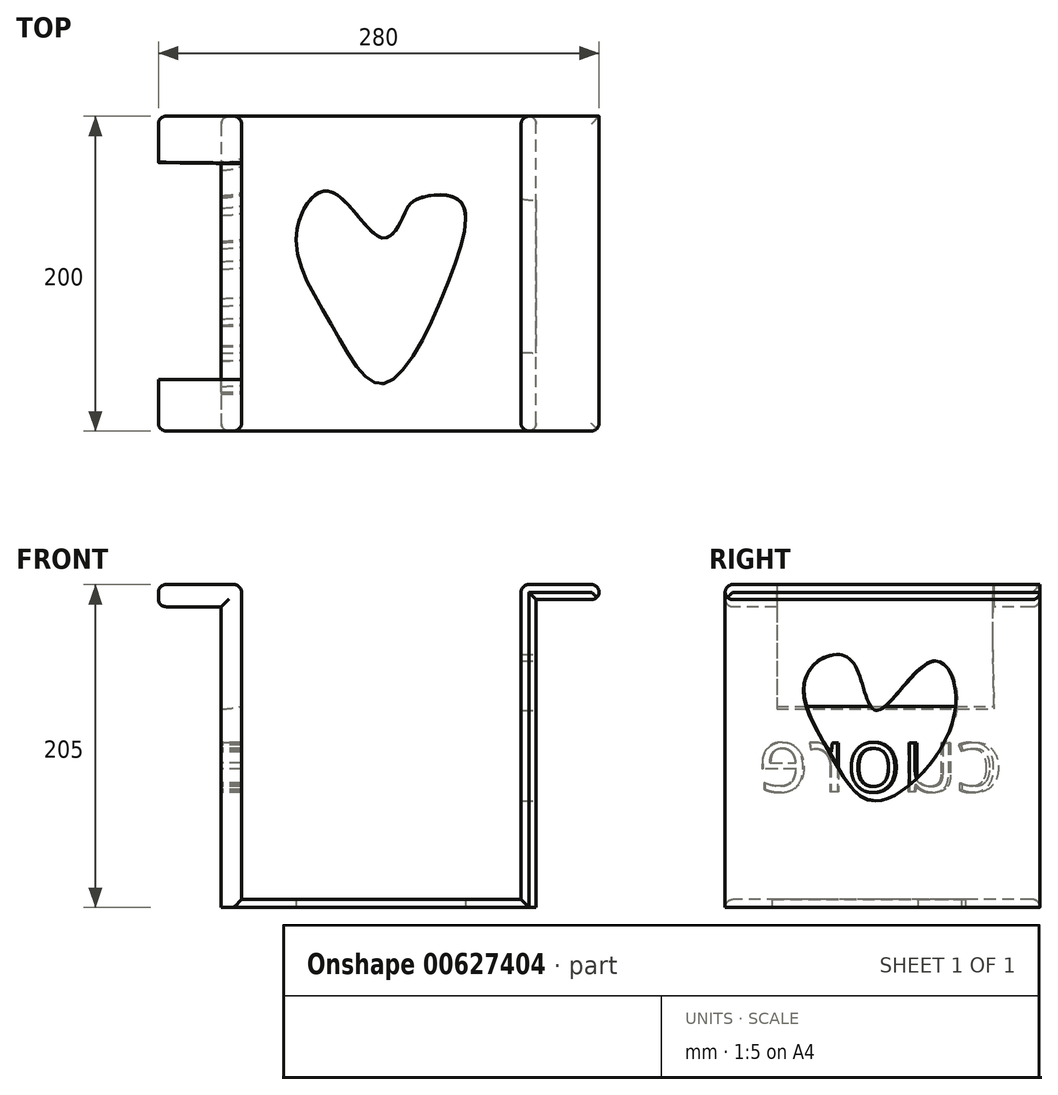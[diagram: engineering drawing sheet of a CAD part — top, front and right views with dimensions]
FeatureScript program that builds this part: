
annotation { "Feature Type Name" : "Feature", "Feature Type Description" : "" }
export const myFeature = defineFeature(function(context is Context, id is Id, definition is map)
    precondition{}
    {
        {
            var Q0;
            Q0=qCreatedBy(makeId("Top.planeOp"),FACE);
            var sketch = newSketch(context, id + "F0", { "sketchPlane" : qUnion([Q0])});
            skLineSegment(sketch, "E0", {"start": v(-102.24, -95.91) * mm, "end": v(97.76, -95.91) * mm});
            skLineSegment(sketch, "E1", {"start": v(97.76, -95.91) * mm, "end": v(97.76, 104.09) * mm});
            skLineSegment(sketch, "E2", {"start": v(97.76, 104.09) * mm, "end": v(-102.24, 104.09) * mm});
            skLineSegment(sketch, "E3", {"start": v(-102.24, 104.09) * mm, "end": v(-102.24, -95.91) * mm});
            skSolve(sketch);
        }
        {
            var Q0;
            Q0=makeQuery(id+"F0.imprint","IMPRINT",FACE,{"disambiguationData":[TD([[makeQuery(id+"F0.imprint","IMPRINT",EDGE,{"derivedFrom":sQuery(id+"F0.wireOp",EDGE,"E0")}),1.0]])]});
            extrude(context, id + "F1", {"entities" : qUnion([Q0]), "depth" : 5 * mm, "offsetDistance" : 25.4 * mm});
        }
        {
            var Q0;
            Q0=makeQuery(id+"F1.opExtrude","CAP_FACE",FACE,{"disambiguationData":[OSD([sQuery(id+"F0.wireOp",EDGE,"E0"),sQuery(id+"F0.wireOp",EDGE,"E1"),sQuery(id+"F0.wireOp",EDGE,"E2"),sQuery(id+"F0.wireOp",EDGE,"E3")])],"isStart":false});
            var sketch = newSketch(context, id + "F2", { "sketchPlane" : qUnion([Q0])});
            skLineSegment(sketch, "E4", {"start": v(88.16, 104.09) * mm, "end": v(88.16, -95.91) * mm});
            skLineSegment(sketch, "E5", {"start": v(88.16, -95.91) * mm, "end": v(97.76, -95.91) * mm});
            skLineSegment(sketch, "E6", {"start": v(97.76, -95.91) * mm, "end": v(97.76, 104.09) * mm});
            skLineSegment(sketch, "E7", {"start": v(97.76, 104.09) * mm, "end": v(88.16, 104.09) * mm});
            skLineSegment(sketch, "E8", {"start": v(-89.36, 104.09) * mm, "end": v(-89.36, -95.91) * mm});
            skLineSegment(sketch, "E9", {"start": v(-89.36, -95.91) * mm, "end": v(-102.24, -95.91) * mm});
            skLineSegment(sketch, "E10", {"start": v(-102.24, -95.91) * mm, "end": v(-102.24, 104.09) * mm});
            skLineSegment(sketch, "E11", {"start": v(-102.24, 104.09) * mm, "end": v(-89.36, 104.09) * mm});
            skSolve(sketch);
        }
        {
            var Q0;
            Q0 = qSketchRegion(id + "F2", true);
            extrude(context, id + "F3", {"entities" : qUnion([Q0]), "operationType" : NewBodyOperationType.ADD, "depth" : 200 * mm, "offsetDistance" : 25.4 * mm});
        }
        {
            var Q0;
            Q0=makeQuery(id+"F3.boolean.opBoolean","MERGE",FACE,{"derivedFrom":[makeQuery(id+"F1.opExtrude","SWEPT_FACE",FACE,{"disambiguationData":[OSD([sQuery(id+"F0.wireOp",EDGE,"E1")])]}),makeQuery(id+"F3.opExtrude","SWEPT_FACE",FACE,{"disambiguationData":[OSD([sQuery(id+"F2.wireOp",EDGE,"E6")])]})]});
            var sketch = newSketch(context, id + "F4", { "sketchPlane" : qUnion([Q0])});
            skLineSegment(sketch, "E12", {"start": v(-95.91, 205) * mm, "end": v(-95.91, 195.43) * mm});
            skLineSegment(sketch, "E13", {"start": v(-95.91, 195.43) * mm, "end": v(104.09, 195.43) * mm});
            skLineSegment(sketch, "E14", {"start": v(104.09, 195.43) * mm, "end": v(104.09, 205) * mm});
            skSolve(sketch);
        }
        {
            var Q0;
            Q0=makeQuery(id+"F4.imprint","IMPRINT",FACE,{"disambiguationData":[TD([[makeQuery(id+"F4.imprint","IMPRINT",EDGE,{"derivedFrom":sQuery(id+"F4.wireOp",EDGE,"E12")}),1.0]])]});
            extrude(context, id + "F5", {"entities" : qUnion([Q0]), "operationType" : NewBodyOperationType.ADD, "depth" : 40 * mm, "offsetDistance" : 25.4 * mm});
        }
        {
            var Q0;
            Q0=makeQuery(id+"F3.boolean.opBoolean","MERGE",FACE,{"derivedFrom":[makeQuery(id+"F1.opExtrude","SWEPT_FACE",FACE,{"disambiguationData":[OSD([sQuery(id+"F0.wireOp",EDGE,"E3")])]}),makeQuery(id+"F3.opExtrude","SWEPT_FACE",FACE,{"disambiguationData":[OSD([sQuery(id+"F2.wireOp",EDGE,"E10")])]})]});
            var sketch = newSketch(context, id + "F6", { "sketchPlane" : qUnion([Q0])});
            skLineSegment(sketch, "E15", {"start": v(-104.09, 190.92) * mm, "end": v(95.91, 190.92) * mm});
            skLineSegment(sketch, "E16", {"start": v(95.91, 190.92) * mm, "end": v(95.91, 205) * mm});
            skLineSegment(sketch, "E17", {"start": v(95.91, 205) * mm, "end": v(-104.09, 205) * mm});
            skLineSegment(sketch, "E18", {"start": v(-104.09, 205) * mm, "end": v(-104.09, 190.92) * mm});
            skSolve(sketch);
        }
        {
            var Q0;
            Q0=makeQuery(id+"F6.imprint","IMPRINT",FACE,{"disambiguationData":[TD([[makeQuery(id+"F6.imprint","IMPRINT",EDGE,{"derivedFrom":sQuery(id+"F6.wireOp",EDGE,"E15")}),1.0]])]});
            extrude(context, id + "F7", {"entities" : qUnion([Q0]), "operationType" : NewBodyOperationType.ADD, "depth" : 40 * mm, "offsetDistance" : 25.4 * mm});
        }
        {
            var Q0;
            Q0=makeQuery(id+"F3.boolean.opBoolean","MERGE",FACE,{"derivedFrom":[makeQuery(id+"F1.opExtrude","SWEPT_FACE",FACE,{"disambiguationData":[OSD([sQuery(id+"F0.wireOp",EDGE,"E1")])]}),makeQuery(id+"F3.opExtrude","SWEPT_FACE",FACE,{"disambiguationData":[OSD([sQuery(id+"F2.wireOp",EDGE,"E6")])]})]});
            var sketch = newSketch(context, id + "F8", { "sketchPlane" : qUnion([Q0])});
            skFitSpline(sketch, "E19", {"points": [v(0, 125.17) * mm, v(-14.77, 155.55) * mm, v(-35.03, 157.65) * mm, v(-46.2, 137.74) * mm, v(-28.4, 95.83) * mm, v(0, 67.54) * mm, v(49.84, 123.07) * mm, v(35.52, 156.25) * mm, v(0, 125.17) * mm]});
            skSolve(sketch);
        }
        {
            var Q0;
            Q0=makeQuery(id+"F8.imprint","IMPRINT",FACE,{"disambiguationData":[TD([[makeQuery(id+"F8.imprint","IMPRINT",EDGE,{"derivedFrom":sQuery(id+"F8.wireOp",EDGE,"E19")}),1.0]])]});
            var Q1;
            Q1=makeQuery(id+"F3.boolean.opBoolean","MERGE",EDGE,{"derivedFrom":[makeQuery(id+"F1.opExtrude","SWEPT_EDGE",EDGE,{"disambiguationData":[OSD([sQuery(id+"F0.wireOp",EDGE,"E1"),sQuery(id+"F0.wireOp",EDGE,"E2")])]}),makeQuery(id+"F3.opExtrude","SWEPT_EDGE",EDGE,{"disambiguationData":[OSD([sQuery(id+"F2.wireOp",EDGE,"E6"),sQuery(id+"F2.wireOp",EDGE,"E7")])]})]});
            revolve(context, id + "F9", {"operationType" : NewBodyOperationType.REMOVE, "entities" : qUnion([Q0]), "axis" : qUnion([Q1]), "revolveType" : RevolveType.FULL, "oppositeDirection" : true});
        }
        {
            var Q0;
            Q0=makeQuery(id+"F3.boolean.opBoolean","MERGE",FACE,{"derivedFrom":[makeQuery(id+"F1.opExtrude","SWEPT_FACE",FACE,{"disambiguationData":[OSD([sQuery(id+"F0.wireOp",EDGE,"E3")])]}),makeQuery(id+"F3.opExtrude","SWEPT_FACE",FACE,{"disambiguationData":[OSD([sQuery(id+"F2.wireOp",EDGE,"E10")])]})]});
            var sketch = newSketch(context, id + "F10", { "sketchPlane" : qUnion([Q0])});
            skText(sketch, "E20", { "text": "cuore", "fontName": "OpenSans-Regular.ttf"});
            const initialGuessF10  = {"E20": [-0.07785, 0.07346, 1, 0, 0.04146]};
            skSetInitialGuess(sketch, initialGuessF10);
            skSolve(sketch);
        }
        {
            var Q0;
            Q0=makeQuery(id+"F10.imprint","IMPRINT",FACE,{"disambiguationData":[TD([[makeQuery(id+"F10.imprint","IMPRINT",EDGE,{"derivedFrom":sQuery(id+"F10.wireOp",EDGE,"E20.sketch_text.stroke-32")}),-1.0]])]});
            var Q1;
            Q1=makeQuery(id+"F10.imprint","IMPRINT",FACE,{"disambiguationData":[TD([[makeQuery(id+"F10.imprint","IMPRINT",EDGE,{"derivedFrom":sQuery(id+"F10.wireOp",EDGE,"E20.sketch_text.stroke-62")}),-1.0]])]});
            var Q2;
            Q2=makeQuery(id+"F10.imprint","IMPRINT",FACE,{"disambiguationData":[TD([[makeQuery(id+"F10.imprint","IMPRINT",EDGE,{"derivedFrom":sQuery(id+"F10.wireOp",EDGE,"E20.sketch_text.stroke-0")}),-1.0]])]});
            var Q3;
            Q3=makeQuery(id+"F10.imprint","IMPRINT",FACE,{"disambiguationData":[TD([[makeQuery(id+"F10.imprint","IMPRINT",EDGE,{"derivedFrom":sQuery(id+"F10.wireOp",EDGE,"E20.sketch_text.stroke-49")}),-1.0]])]});
            var Q4;
            Q4=makeQuery(id+"F10.imprint","IMPRINT",FACE,{"disambiguationData":[TD([[makeQuery(id+"F10.imprint","IMPRINT",EDGE,{"derivedFrom":sQuery(id+"F10.wireOp",EDGE,"E20.sketch_text.stroke-15")}),-1.0]])]});
            var Q5;
            Q5=makeQuery(id+"F3.boolean.opBoolean","MERGE",EDGE,{"derivedFrom":[makeQuery(id+"F1.opExtrude","SWEPT_EDGE",EDGE,{"disambiguationData":[OSD([sQuery(id+"F0.wireOp",EDGE,"E2"),sQuery(id+"F0.wireOp",EDGE,"E3")])]}),makeQuery(id+"F3.opExtrude","SWEPT_EDGE",EDGE,{"disambiguationData":[OSD([sQuery(id+"F2.wireOp",EDGE,"E10"),sQuery(id+"F2.wireOp",EDGE,"E11")])]})]});
            revolve(context, id + "F11", {"operationType" : NewBodyOperationType.REMOVE, "entities" : qUnion([Q0, Q1, Q2, Q3, Q4]), "axis" : qUnion([Q5]), "revolveType" : RevolveType.FULL, "oppositeDirection" : true});
        }
        {
            var Q0;
            {var subQ0=sQuery(id+"F2.wireOp",EDGE,"E4");Q0=makeQuery(id+"F2.imprint","IMPRINT",FACE,{"disambiguationData":[TD([[makeQuery(id+"F2.imprint","IMPRINT",EDGE,{"derivedFrom":subQ0}),-1.0]])]});}
            var sketch = newSketch(context, id + "F12", { "sketchPlane" : qUnion([Q0])});
            skFitSpline(sketch, "E21", {"points": [v(0, 26.75) * mm, v(-33.62, 56.39) * mm, v(-54.54, 29.54) * mm, v(-32.58, -27.99) * mm, v(0, -66) * mm, v(42.39, 0) * mm, v(48.66, 50.8) * mm, v(21.47, 51.16) * mm, v(13.45, 40.7) * mm, v(0, 26.75) * mm]});
            skSolve(sketch);
        }
        {
            var Q0;
            Q0=makeQuery(id+"F12.imprint","IMPRINT",FACE,{"disambiguationData":[TD([[makeQuery(id+"F12.imprint","IMPRINT",EDGE,{"derivedFrom":sQuery(id+"F12.wireOp",EDGE,"E21")}),1.0]])]});
            var Q1;
            Q1=makeQuery(id+"F1.opExtrude","CAP_EDGE",EDGE,{"disambiguationData":[OSD([sQuery(id+"F0.wireOp",EDGE,"E0")])],"isStart":false});
            revolve(context, id + "F13", {"operationType" : NewBodyOperationType.REMOVE, "entities" : qUnion([Q0]), "axis" : qUnion([Q1]), "revolveType" : RevolveType.FULL, "oppositeDirection" : true});
        }
        {
            var Q0;
            Q0=makeQuery(id+"F7.opExtrude","CAP_EDGE",EDGE,{"disambiguationData":[OSD([sQuery(id+"F6.wireOp",EDGE,"E17")])],"isStart":false});
            var Q1;
            Q1=makeQuery(id+"F7.opExtrude","CAP_EDGE",EDGE,{"disambiguationData":[OSD([sQuery(id+"F6.wireOp",EDGE,"E15")])],"isStart":false});
            fillet(context, id + "F14", {"entities" : qUnion([Q0, Q1]), "radius" : 5 * mm, "tangentPropagation" : true, "allowEdgeOverflow" : false});
        }
        {
            var Q0;
            Q0=makeQuery(id+"F3.boolean.opBoolean","MERGE",EDGE,{"derivedFrom":[makeQuery(id+"F1.opExtrude","SWEPT_EDGE",EDGE,{"disambiguationData":[OSD([sQuery(id+"F0.wireOp",EDGE,"E1"),sQuery(id+"F0.wireOp",EDGE,"E2")])]}),makeQuery(id+"F3.opExtrude","SWEPT_EDGE",EDGE,{"disambiguationData":[OSD([sQuery(id+"F2.wireOp",EDGE,"E6"),sQuery(id+"F2.wireOp",EDGE,"E7")])]})]});
            var Q1;
            Q1=makeQuery(id+"F3.boolean.opBoolean","MERGE",EDGE,{"derivedFrom":[makeQuery(id+"F1.opExtrude","SWEPT_EDGE",EDGE,{"disambiguationData":[OSD([sQuery(id+"F0.wireOp",EDGE,"E2"),sQuery(id+"F0.wireOp",EDGE,"E3")])]}),makeQuery(id+"F3.opExtrude","SWEPT_EDGE",EDGE,{"disambiguationData":[OSD([sQuery(id+"F2.wireOp",EDGE,"E10"),sQuery(id+"F2.wireOp",EDGE,"E11")])]})]});
            fillet(context, id + "F15", {"entities" : qUnion([Q0, Q1]), "radius" : 5 * mm, "tangentPropagation" : true, "allowEdgeOverflow" : false});
        }
        {
            var Q0;
            Q0=makeQuery(id+"F3.opExtrude","SWEPT_EDGE",EDGE,{"disambiguationData":[OSD([sQuery(id+"F0.wireOp",EDGE,"E2"),sQuery(id+"F2.wireOp",EDGE,"E8"),sQuery(id+"F2.wireOp",EDGE,"E11")])]});
            fillet(context, id + "F16", {"entities" : qUnion([Q0]), "radius" : 5 * mm, "tangentPropagation" : true, "allowEdgeOverflow" : false});
        }
        {
            var Q0;
            Q0=makeQuery(id+"F3.boolean.opBoolean","MERGE",EDGE,{"derivedFrom":[makeQuery(id+"F1.opExtrude","SWEPT_EDGE",EDGE,{"disambiguationData":[OSD([sQuery(id+"F0.wireOp",EDGE,"E0"),sQuery(id+"F0.wireOp",EDGE,"E3")])]}),makeQuery(id+"F3.opExtrude","SWEPT_EDGE",EDGE,{"disambiguationData":[OSD([sQuery(id+"F2.wireOp",EDGE,"E9"),sQuery(id+"F2.wireOp",EDGE,"E10")])]})]});
            fillet(context, id + "F17", {"entities" : qUnion([Q0]), "radius" : 5 * mm, "tangentPropagation" : true, "allowEdgeOverflow" : false});
        }
        {
            var Q0;
            Q0=makeQuery(id+"F3.opExtrude","SWEPT_EDGE",EDGE,{"disambiguationData":[OSD([sQuery(id+"F0.wireOp",EDGE,"E0"),sQuery(id+"F2.wireOp",EDGE,"E8"),sQuery(id+"F2.wireOp",EDGE,"E9")])]});
            fillet(context, id + "F18", {"entities" : qUnion([Q0]), "radius" : 5 * mm, "tangentPropagation" : true, "allowEdgeOverflow" : false});
        }
        {
            var Q0;
            Q0=makeQuery(id+"F3.opExtrude","SWEPT_EDGE",EDGE,{"disambiguationData":[OSD([sQuery(id+"F0.wireOp",EDGE,"E0"),sQuery(id+"F2.wireOp",EDGE,"E4"),sQuery(id+"F2.wireOp",EDGE,"E5")])]});
            fillet(context, id + "F19", {"entities" : qUnion([Q0]), "radius" : 5 * mm, "tangentPropagation" : true, "allowEdgeOverflow" : false});
        }
        {
            var Q0;
            Q0=makeQuery(id+"F1.opExtrude","CAP_EDGE",EDGE,{"disambiguationData":[OSD([sQuery(id+"F0.wireOp",EDGE,"E0")])],"isStart":false});
            fillet(context, id + "F20", {"entities" : qUnion([Q0]), "radius" : 5 * mm, "tangentPropagation" : true, "allowEdgeOverflow" : false});
        }
        {
            var Q0;
            Q0=makeQuery(id+"F3.opExtrude","SWEPT_EDGE",EDGE,{"disambiguationData":[OSD([sQuery(id+"F0.wireOp",EDGE,"E2"),sQuery(id+"F2.wireOp",EDGE,"E4"),sQuery(id+"F2.wireOp",EDGE,"E7")])]});
            var Q1;
            Q1=makeQuery(id+"F7.boolean.opBoolean","MERGE",FACE,{"derivedFrom":[makeQuery(id+"F3.opExtrude","CAP_FACE",FACE,{"disambiguationData":[OSD([sQuery(id+"F2.wireOp",EDGE,"E8"),sQuery(id+"F2.wireOp",EDGE,"E9"),sQuery(id+"F2.wireOp",EDGE,"E10"),sQuery(id+"F2.wireOp",EDGE,"E11")])],"isStart":false}),makeQuery(id+"F7.opExtrude","SWEPT_FACE",FACE,{"disambiguationData":[OSD([sQuery(id+"F6.wireOp",EDGE,"E17")])]})]});
            fillet(context, id + "F21", {"entities" : qUnion([Q0, Q1]), "radius" : 5 * mm, "tangentPropagation" : true, "allowEdgeOverflow" : false});
        }
        {
            var Q0;
            Q0=makeQuery(id+"F1.opExtrude","CAP_EDGE",EDGE,{"disambiguationData":[OSD([sQuery(id+"F0.wireOp",EDGE,"E2")])],"isStart":false});
            fillet(context, id + "F22", {"entities" : qUnion([Q0]), "radius" : 5 * mm, "tangentPropagation" : true, "allowEdgeOverflow" : false});
        }
        {
            var Q0;
            Q0=makeQuery(id+"F5.opExtrude","SWEPT_EDGE",EDGE,{"disambiguationData":[OSD([sQuery(id+"F0.wireOp",EDGE,"E1"),sQuery(id+"F0.wireOp",EDGE,"E2"),sQuery(id+"F2.wireOp",EDGE,"E6"),sQuery(id+"F2.wireOp",EDGE,"E7"),sQuery(id+"F4.wireOp",EDGE,"E13"),sQuery(id+"F4.wireOp",EDGE,"E14")])]});
            fillet(context, id + "F23", {"entities" : qUnion([Q0]), "radius" : 5 * mm, "tangentPropagation" : true, "allowEdgeOverflow" : false});
        }
        {
            var Q0;
            Q0=makeQuery(id+"F5.boolean.opBoolean","MERGE",EDGE,{"derivedFrom":[makeQuery(id+"F3.opExtrude","CAP_EDGE",EDGE,{"disambiguationData":[OSD([sQuery(id+"F2.wireOp",EDGE,"E5")])],"isStart":false}),makeQuery(id+"F5.opExtrude","SWEPT_EDGE",EDGE,{"disambiguationData":[OSD([sQuery(id+"F2.wireOp",EDGE,"E6"),sQuery(id+"F4.wireOp",EDGE,"E12")])]})]});
            fillet(context, id + "F24", {"entities" : qUnion([Q0]), "radius" : 5 * mm, "tangentPropagation" : true, "allowEdgeOverflow" : false});
        }
        {
            var Q0;
            Q0=makeQuery(id+"F5.opExtrude","CAP_EDGE",EDGE,{"disambiguationData":[OSD([sQuery(id+"F2.wireOp",EDGE,"E6")])],"isStart":false});
            fillet(context, id + "F25", {"entities" : qUnion([Q0]), "radius" : 5 * mm, "tangentPropagation" : true, "allowEdgeOverflow" : false});
        }
        {
            var Q0;
            Q0=makeQuery(id+"F3.boolean.opBoolean","MERGE",EDGE,{"derivedFrom":[makeQuery(id+"F1.opExtrude","SWEPT_EDGE",EDGE,{"disambiguationData":[OSD([sQuery(id+"F0.wireOp",EDGE,"E0"),sQuery(id+"F0.wireOp",EDGE,"E1")])]}),makeQuery(id+"F3.opExtrude","SWEPT_EDGE",EDGE,{"disambiguationData":[OSD([sQuery(id+"F2.wireOp",EDGE,"E5"),sQuery(id+"F2.wireOp",EDGE,"E6")])]})]});
            fillet(context, id + "F26", {"entities" : qUnion([Q0]), "radius" : 5 * mm, "tangentPropagation" : true, "allowEdgeOverflow" : false});
        }
        {
            var Q0;
            Q0=makeQuery(id+"F5.opExtrude","SWEPT_EDGE",EDGE,{"disambiguationData":[OSD([sQuery(id+"F0.wireOp",EDGE,"E0"),sQuery(id+"F0.wireOp",EDGE,"E1"),sQuery(id+"F2.wireOp",EDGE,"E5"),sQuery(id+"F2.wireOp",EDGE,"E6"),sQuery(id+"F4.wireOp",EDGE,"E12"),sQuery(id+"F4.wireOp",EDGE,"E13")])]});
            fillet(context, id + "F27", {"entities" : qUnion([Q0]), "radius" : 5 * mm, "allowEdgeOverflow" : false});
        }
        {
            var Q0;
            Q0=makeQuery(id+"F5.opExtrude","CAP_EDGE",EDGE,{"disambiguationData":[OSD([sQuery(id+"F4.wireOp",EDGE,"E13")])],"isStart":false});
            fillet(context, id + "F28", {"entities" : qUnion([Q0]), "radius" : 5 * mm, "allowEdgeOverflow" : false});
        }
        {
            var Q0;
            {var subQ0=sQuery(id+"F0.wireOp",EDGE,"E0");var subQ1=sQuery(id+"F0.wireOp",EDGE,"E3");Q0=makeQuery(id+"F11.boolean.opBoolean","SPLIT",FACE,{"disambiguationData":[TD([makeQuery(id+"F1.opExtrude","SWEPT_FACE",FACE,{"disambiguationData":[OSD([subQ0])]})])],"derivedFrom":makeQuery(id+"F3.boolean.opBoolean","MERGE",FACE,{"derivedFrom":[makeQuery(id+"F1.opExtrude","SWEPT_FACE",FACE,{"disambiguationData":[OSD([subQ1])]}),makeQuery(id+"F3.opExtrude","SWEPT_FACE",FACE,{"disambiguationData":[OSD([sQuery(id+"F2.wireOp",EDGE,"E10")])]})]})});}
            var sketch = newSketch(context, id + "F29", { "sketchPlane" : qUnion([Q0])});
            skLineSegment(sketch, "E22", {"start": v(-74.87, 126) * mm, "end": v(63.1, 126) * mm});
            skLineSegment(sketch, "E23", {"start": v(63.1, 126) * mm, "end": v(63.1, 174.9) * mm});
            skLineSegment(sketch, "E24", {"start": v(63.1, 174.9) * mm, "end": v(-73.79, 174.9) * mm});
            skLineSegment(sketch, "E25", {"start": v(-73.79, 174.9) * mm, "end": v(-74.87, 126) * mm});
            skSolve(sketch);
        }
        {
            var Q0;
            Q0=makeQuery(id+"F29.imprint","IMPRINT",FACE,{"disambiguationData":[TD([[makeQuery(id+"F29.imprint","IMPRINT",EDGE,{"derivedFrom":sQuery(id+"F29.wireOp",EDGE,"E22")}),1.0]])]});
            var Q1;
            Q1=sQuery(id+"F29.wireOp",EDGE,"E24");
            revolve(context, id + "F30", {"operationType" : NewBodyOperationType.REMOVE, "entities" : qUnion([Q0]), "axis" : qUnion([Q1]), "revolveType" : RevolveType.FULL, "oppositeDirection" : true});
        }
    });
